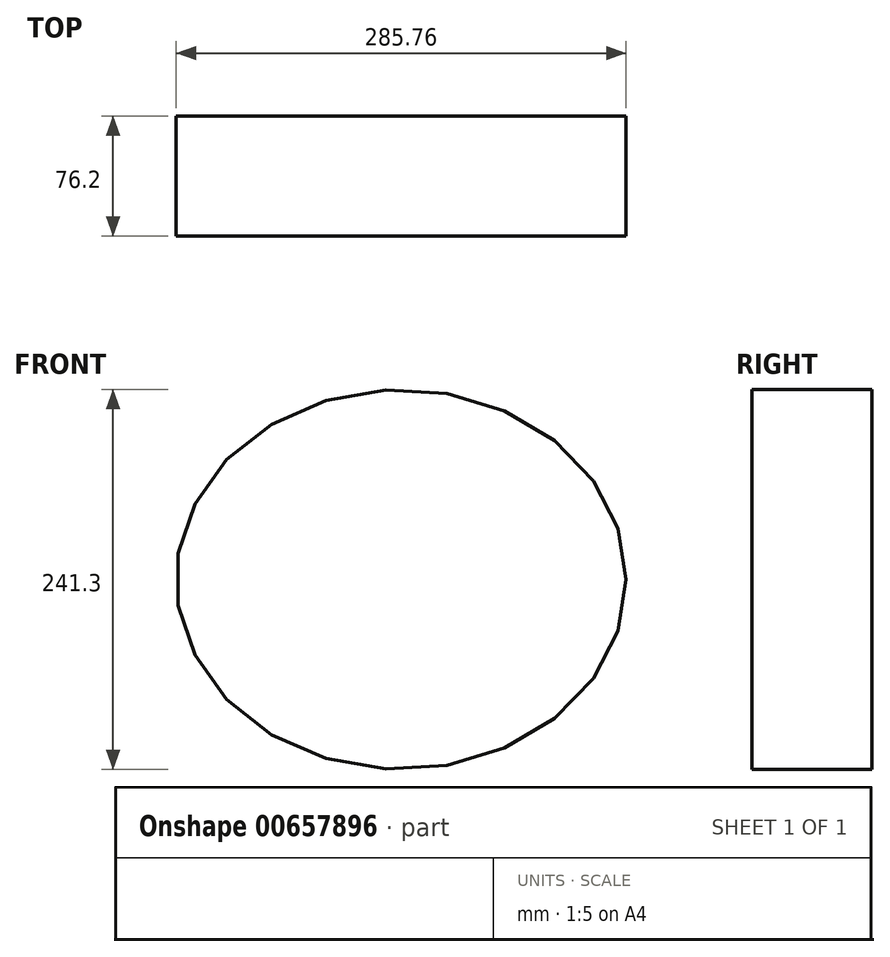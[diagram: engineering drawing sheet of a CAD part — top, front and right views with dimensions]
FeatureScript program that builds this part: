
annotation { "Feature Type Name" : "Feature", "Feature Type Description" : "" }
export const myFeature = defineFeature(function(context is Context, id is Id, definition is map)
    precondition{}
    {
        {
            var Q0;
            Q0=qCreatedBy(makeId("Front.planeOp"),FACE);
            var sketch = newSketch(context, id + "F0", { "sketchPlane" : qUnion([Q0])});
            skEllipse(sketch, "E0", {"center": v(0, 0) * mm, "majorRadius": 142.88 * mm, "minorRadius": 120.65 * mm, "majorAxis": v(1, 0)});
            skSolve(sketch);
        }
        {
            var Q0;
            Q0 = qSketchRegion(id + "F0", true);
            extrude(context, id + "F1", {"entities" : qUnion([Q0]), "depth" : 76.2 * mm, "offsetDistance" : 25.4 * mm});
        }
    });
